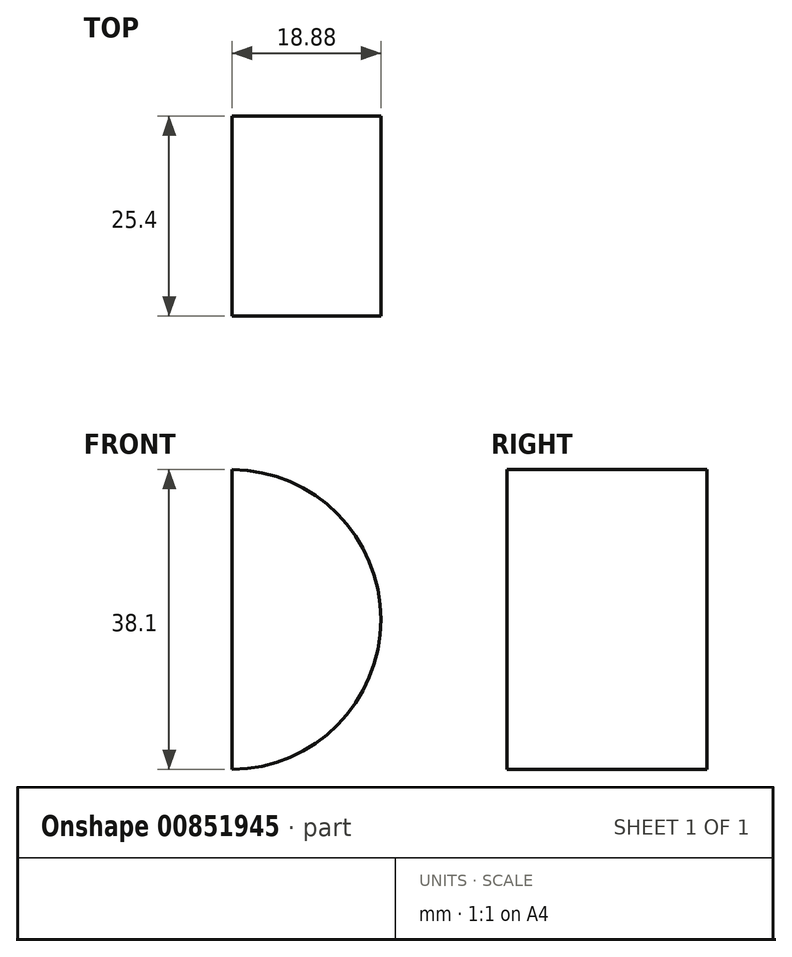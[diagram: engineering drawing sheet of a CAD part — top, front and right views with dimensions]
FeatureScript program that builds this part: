
annotation { "Feature Type Name" : "Feature", "Feature Type Description" : "" }
export const myFeature = defineFeature(function(context is Context, id is Id, definition is map)
    precondition{}
    {
        {
            var Q0;
            Q0=qCreatedBy(makeId("Front.planeOp"),FACE);
            var sketch = newSketch(context, id + "F0", { "sketchPlane" : qUnion([Q0])});
            skLineSegment(sketch, "E0", {"start": v(-1.92, -3.58) * mm, "end": v(-1.92, 34.52) * mm});
            skLineSegment(sketch, "E1", {"start": v(-1.92, 34.52) * mm, "end": v(-1.92, 15.47) * mm});
            skArc(sketch, "E2", {"start": v(-1.92, -3.58) * mm, "mid": v(16.96, 15.47) * mm, "end": v(-1.92, 34.52) * mm});
            skSolve(sketch);
        }
        {
            var Q0;
            Q0 = qSketchRegion(id + "F0", true);
            extrude(context, id + "F1", {"entities" : qUnion([Q0]), "depth" : 25.4 * mm, "offsetDistance" : 25.4 * mm});
        }
    });
